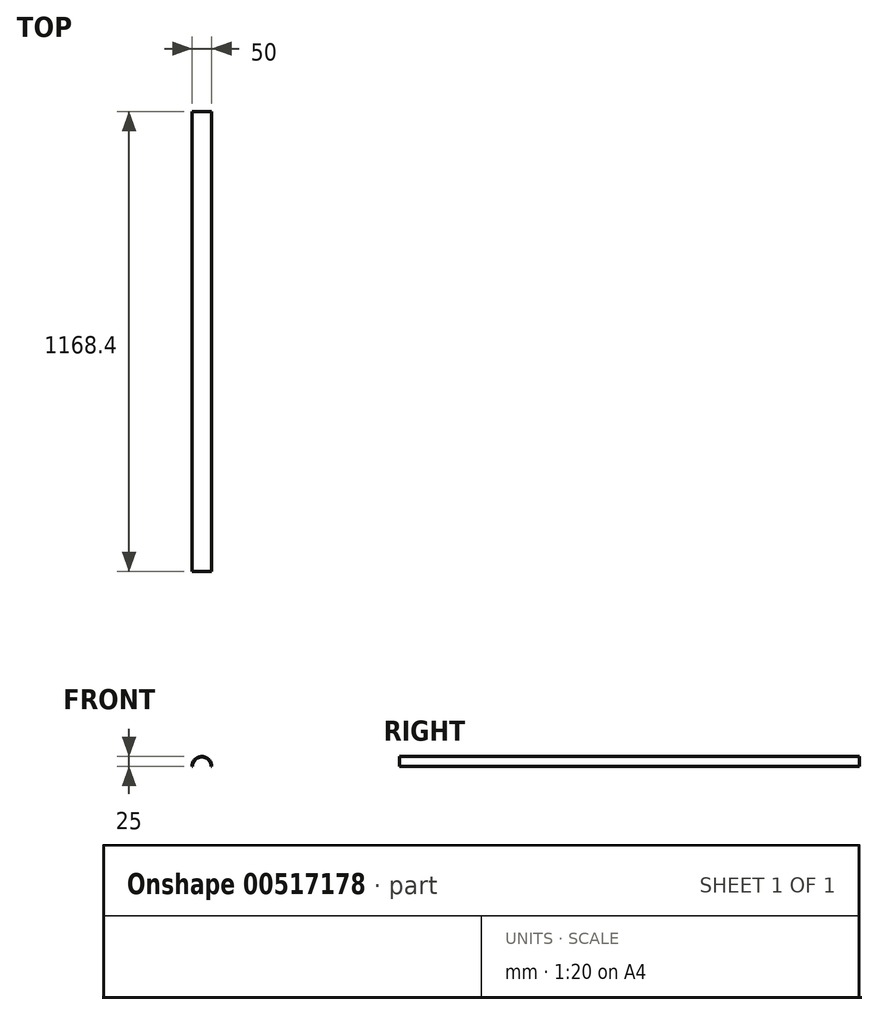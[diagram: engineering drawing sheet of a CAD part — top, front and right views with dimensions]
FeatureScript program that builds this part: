
annotation { "Feature Type Name" : "Feature", "Feature Type Description" : "" }
export const myFeature = defineFeature(function(context is Context, id is Id, definition is map)
    precondition{}
    {
        {
            var Q0;
            Q0=qCreatedBy(makeId("Front.planeOp"),FACE);
            var sketch = newSketch(context, id + "F0", { "sketchPlane" : qUnion([Q0])});
            skArc(sketch, "E0", {"start": v(25, 0) * mm, "mid": v(0, 25) * mm, "end": v(-25, 0) * mm});
            skArc(sketch, "E1", {"start": v(23.48, 0) * mm, "mid": v(0, 23.56) * mm, "end": v(-23.48, 0) * mm});
            skLineSegment(sketch, "E2", {"start": v(-25, 0) * mm, "end": v(-23.48, 0) * mm});
            skLineSegment(sketch, "E3", {"start": v(23.48, 0) * mm, "end": v(25, 0) * mm});
            skSolve(sketch);
        }
        {
            var Q0;
            Q0 = qSketchRegion(id + "F0", true);
            extrude(context, id + "F1", {"entities" : qUnion([Q0]), "depth" : 1168.4 * mm, "offsetDistance" : 25.4 * mm});
        }
    });
